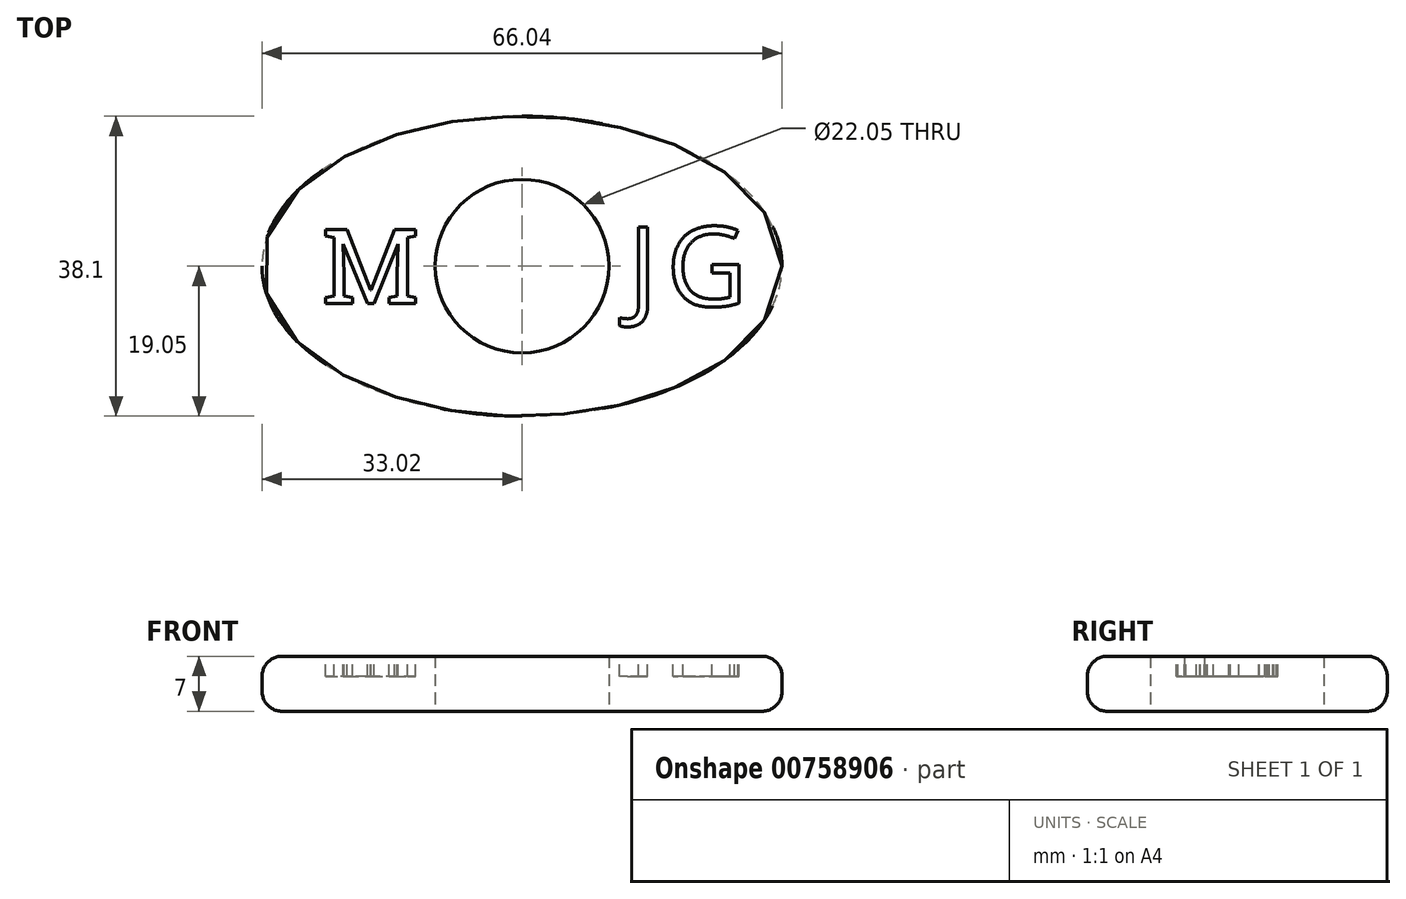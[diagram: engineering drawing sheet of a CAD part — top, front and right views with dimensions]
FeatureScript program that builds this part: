
annotation { "Feature Type Name" : "Feature", "Feature Type Description" : "" }
export const myFeature = defineFeature(function(context is Context, id is Id, definition is map)
    precondition{}
    {
        {
            var Q0;
            Q0=qCreatedBy(makeId("Top.planeOp"),FACE);
            var sketch = newSketch(context, id + "F0", { "sketchPlane" : qUnion([Q0])});
            skEllipse(sketch, "E0", {"center": v(0, 0) * mm, "majorRadius": 33.02 * mm, "minorRadius": 19.05 * mm, "majorAxis": v(1, 0)});
            skCircle(sketch, "E1", {"center": v(0, 0) * mm, "radius": 11.03 * mm});
            skLineSegment(sketch, "E2", {"start": v(-33.02, 0) * mm, "end": v(33.02, 0) * mm, "construction": true});
            skLineSegment(sketch, "E3", {"start": v(0, 19.05) * mm, "end": v(0, -19.05) * mm, "construction": true});
            skSolve(sketch);
        }
        {
            var Q0;
            Q0=makeQuery(id+"F0.imprint","IMPRINT",FACE,{"disambiguationData":[TD([[makeQuery(id+"F0.imprint","IMPRINT",EDGE,{"derivedFrom":sQuery(id+"F0.wireOp",EDGE,"E0")}),1.0]])]});
            extrude(context, id + "F1", {"entities" : qUnion([Q0]), "depth" : 7 * mm, "offsetDistance" : 25.4 * mm});
        }
        {
            var Q0;
            Q0=makeQuery(id+"F1.opExtrude","CAP_EDGE",EDGE,{"disambiguationData":[OSD([sQuery(id+"F0.wireOp",EDGE,"E0")])],"isStart":false});
            var Q1;
            Q1=makeQuery(id+"F1.opExtrude","CAP_EDGE",EDGE,{"disambiguationData":[OSD([sQuery(id+"F0.wireOp",EDGE,"E0")])],"isStart":true});
            fillet(context, id + "F2", {"entities" : qUnion([Q0, Q1]), "radius" : 2.54 * mm, "tangentPropagation" : true, "allowEdgeOverflow" : false});
        }
        {
            var Q0;
            Q0=makeQuery(id+"F1.opExtrude","CAP_FACE",FACE,{"disambiguationData":[OSD([sQuery(id+"F0.wireOp",EDGE,"E0"),sQuery(id+"F0.wireOp",EDGE,"E1")])],"isStart":false});
            var sketch = newSketch(context, id + "F3", { "sketchPlane" : qUnion([Q0])});
            skSolve(sketch);
        }
        {
            var Q0;
            {var subQ0=sQuery(id+"F0.wireOp",EDGE,"E1");Q0=makeQuery(id+"F3.imprint","IMPRINT",FACE,{"disambiguationData":[TD([[makeQuery(id+"F3.imprint","IMPRINT",EDGE,{"derivedFrom":makeQuery(id+"F1.opExtrude","CAP_EDGE",EDGE,{"disambiguationData":[OSD([subQ0])],"isStart":false})}),-1.0]])]});}
            var sketch = newSketch(context, id + "F4", { "sketchPlane" : qUnion([Q0])});
            skText(sketch, "E4", { "text": "M", "fontName": "RobotoSlab-Regular.ttf"});
            skLineSegment(sketch, "E5", {"start": v(0, 0) * mm, "end": v(-25.4, 0) * mm, "construction": true});
            skLineSegment(sketch, "E6", {"start": v(-25.4, 0) * mm, "end": v(-12.7, 0) * mm, "construction": true});
            skPoint(sketch, "E7", {"position": v(19.05, 0) * mm});
            skPoint(sketch, "E8", {"position": v(-19.05, 0) * mm});
            skText(sketch, "E9", { "text": "J", "fontName": "OpenSans-Regular.ttf"});
            skText(sketch, "E10", { "text": "G", "fontName": "OpenSans-Regular.ttf"});
            skLineSegment(sketch, "E11", {"start": v(13.47, 0) * mm, "end": v(17.96, 0) * mm, "construction": true});
            skPoint(sketch, "E12", {"position": v(15.71, 0) * mm});
            skPoint(sketch, "E13", {"position": v(23.42, 0) * mm});
            const initialGuessF4  = {"E4": [-0.0254, -0.00477, 1, 0, 0.00955], "E9": [0.01347, -0.00508, 1, 0, 0.01016], "E10": [0.01834, -0.00508, 1, 0, 0.01016]};
            skSetInitialGuess(sketch, initialGuessF4);
            skSolve(sketch);
        }
        {
            var Q0;
            Q0=qSketchRegion(id+"F4",true);
            extrude(context, id + "F5", {"entities" : qUnion([Q0]), "operationType" : NewBodyOperationType.REMOVE, "oppositeDirection" : true, "depth" : 2.54 * mm, "offsetDistance" : 25.4 * mm});
        }
    });
